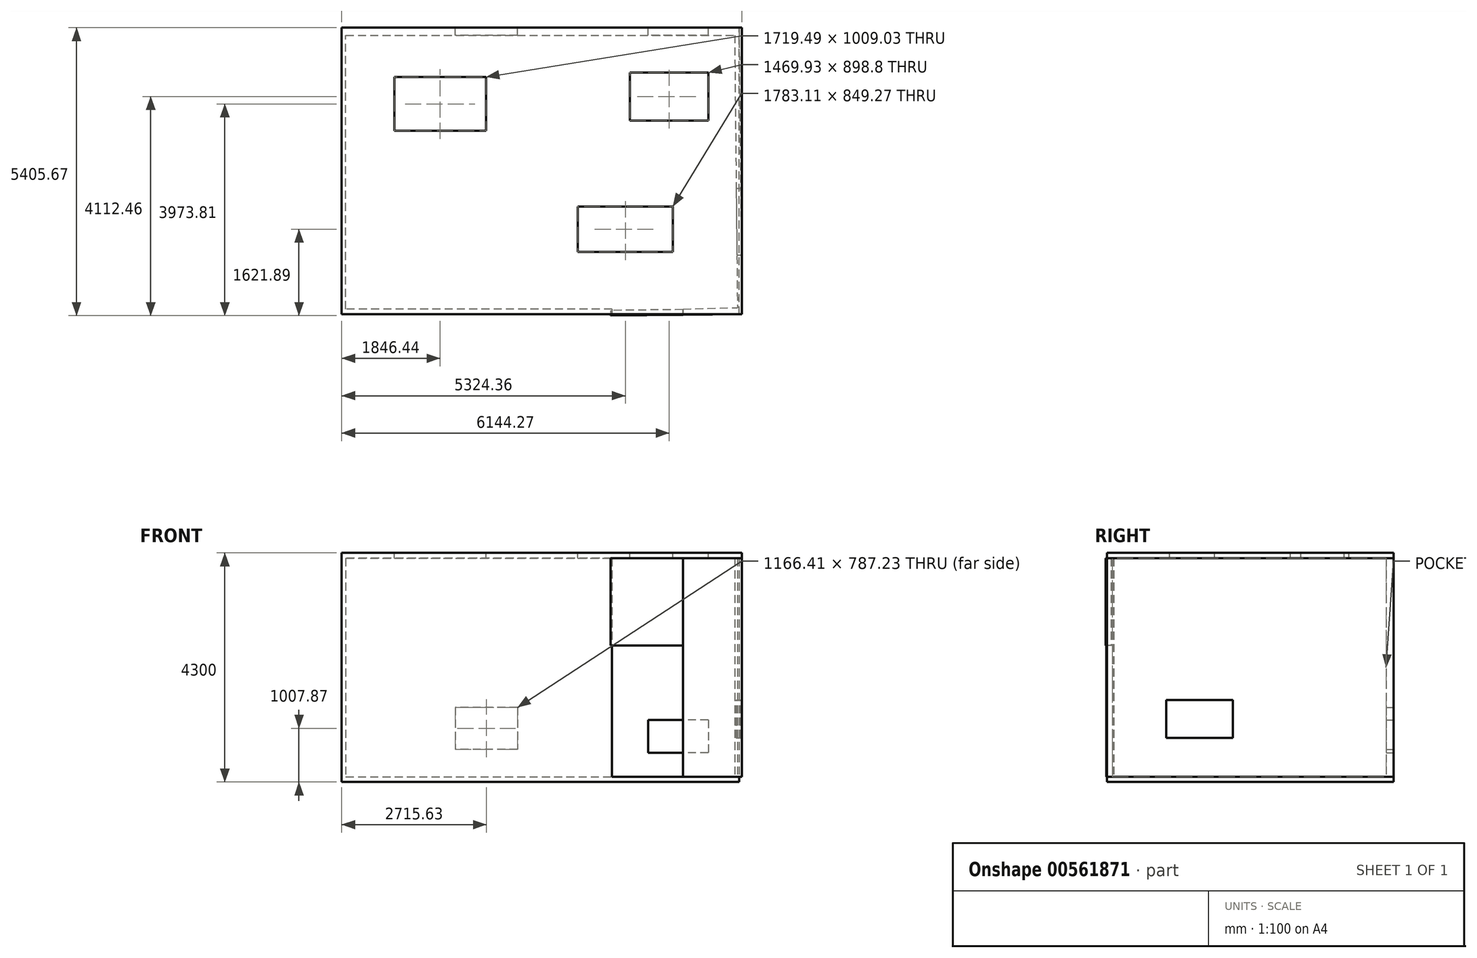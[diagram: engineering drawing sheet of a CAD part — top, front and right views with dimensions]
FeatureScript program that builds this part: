
annotation { "Feature Type Name" : "Feature", "Feature Type Description" : "" }
export const myFeature = defineFeature(function(context is Context, id is Id, definition is map)
    precondition{}
    {
        {
            var Q0;
            Q0=qCreatedBy(makeId("Top.planeOp"),FACE);
            var sketch = newSketch(context, id + "F0", { "sketchPlane" : qUnion([Q0])});
            skLineSegment(sketch, "E0", {"start": v(2012.95, -2660.95) * mm, "end": v(2012.95, -2759.71) * mm});
            skLineSegment(sketch, "E1", {"start": v(2012.95, -2759.71) * mm, "end": v(-3059.37, -2759.71) * mm});
            skLineSegment(sketch, "E2", {"start": v(-3059.37, -2759.71) * mm, "end": v(-3059.37, 2620.12) * mm});
            skLineSegment(sketch, "E3", {"start": v(-3059.37, 2620.12) * mm, "end": v(4397.09, 2620.12) * mm});
            skLineSegment(sketch, "E4", {"start": v(4397.09, 2620.12) * mm, "end": v(4453.48, -2759.71) * mm});
            skLineSegment(sketch, "E5", {"start": v(4453.48, -2759.71) * mm, "end": v(3345.91, -2771.33) * mm});
            skLineSegment(sketch, "E6", {"start": v(3345.91, -2771.33) * mm, "end": v(3345.91, -2660.95) * mm});
            skLineSegment(sketch, "E7", {"start": v(2012.95, -2660.95) * mm, "end": v(-2982.58, -2660.95) * mm});
            skLineSegment(sketch, "E8", {"start": v(-2982.58, -2660.95) * mm, "end": v(-2982.58, -764.97) * mm});
            skLineSegment(sketch, "E9", {"start": v(-2982.58, -764.97) * mm, "end": v(-2982.58, 2477.46) * mm});
            skLineSegment(sketch, "E10", {"start": v(-2982.58, 2477.46) * mm, "end": v(4314.13, 2477.46) * mm});
            skLineSegment(sketch, "E11", {"start": v(4314.13, 2477.46) * mm, "end": v(4367.73, -2634.86) * mm});
            skLineSegment(sketch, "E12", {"start": v(3345.91, -2660.95) * mm, "end": v(4367.73, -2634.86) * mm});
            skSolve(sketch);
        }
        {
            var Q0;
            Q0 = qSketchRegion(id + "F0", true);
            extrude(context, id + "F1", {"entities" : qUnion([Q0]), "depth" : 4100 * mm, "offsetDistance" : 25.4 * mm});
        }
        {
            var Q0;
            Q0=makeQuery(id+"F1.opExtrude","CAP_FACE",FACE,{"disambiguationData":[OSD([sQuery(id+"F0.wireOp",EDGE,"E0"),sQuery(id+"F0.wireOp",EDGE,"E1"),sQuery(id+"F0.wireOp",EDGE,"E2"),sQuery(id+"F0.wireOp",EDGE,"E3"),sQuery(id+"F0.wireOp",EDGE,"E4"),sQuery(id+"F0.wireOp",EDGE,"E5"),sQuery(id+"F0.wireOp",EDGE,"E6"),sQuery(id+"F0.wireOp",EDGE,"E7"),sQuery(id+"F0.wireOp",EDGE,"E8"),sQuery(id+"F0.wireOp",EDGE,"E9"),sQuery(id+"F0.wireOp",EDGE,"E10"),sQuery(id+"F0.wireOp",EDGE,"E11"),sQuery(id+"F0.wireOp",EDGE,"E12")])],"isStart":false});
            var sketch = newSketch(context, id + "F2", { "sketchPlane" : qUnion([Q0])});
            skLineSegment(sketch, "E13.bottom", {"start": v(-3059.37, 2620.12) * mm, "end": v(4453.48, 2620.12) * mm});
            skLineSegment(sketch, "E13.top", {"start": v(-3059.37, -2759.71) * mm, "end": v(4453.48, -2759.71) * mm});
            skLineSegment(sketch, "E13.left", {"start": v(-3059.37, 2620.12) * mm, "end": v(-3059.37, -2759.71) * mm});
            skLineSegment(sketch, "E13.right", {"start": v(4453.48, 2620.12) * mm, "end": v(4453.48, -2759.71) * mm});
            skSolve(sketch);
        }
        {
            var Q0;
            Q0 = qSketchRegion(id + "F2", true);
            extrude(context, id + "F3", {"entities" : qUnion([Q0]), "operationType" : NewBodyOperationType.ADD, "depth" : 100 * mm, "offsetDistance" : 25.4 * mm});
        }
        {
            var Q0;
            Q0=makeQuery(id+"F3.opExtrude","CAP_FACE",FACE,{"disambiguationData":[OSD([sQuery(id+"F2.wireOp",EDGE,"E13.bottom"),sQuery(id+"F2.wireOp",EDGE,"E13.top"),sQuery(id+"F2.wireOp",EDGE,"E13.left"),sQuery(id+"F2.wireOp",EDGE,"E13.right")])],"isStart":false});
            var sketch = newSketch(context, id + "F4", { "sketchPlane" : qUnion([Q0])});
            skLineSegment(sketch, "E14.bottom", {"start": v(1373.43, -739.03) * mm, "end": v(3156.55, -739.03) * mm});
            skLineSegment(sketch, "E14.top", {"start": v(1373.43, -1588.3) * mm, "end": v(3156.55, -1588.3) * mm});
            skLineSegment(sketch, "E14.left", {"start": v(1373.43, -739.03) * mm, "end": v(1373.43, -1588.3) * mm});
            skLineSegment(sketch, "E14.right", {"start": v(3156.55, -739.03) * mm, "end": v(3156.55, -1588.3) * mm});
            skLineSegment(sketch, "E15.bottom", {"start": v(-2072.68, 1692.78) * mm, "end": v(-353.18, 1692.78) * mm});
            skLineSegment(sketch, "E15.top", {"start": v(-2072.68, 683.75) * mm, "end": v(-353.18, 683.75) * mm});
            skLineSegment(sketch, "E15.left", {"start": v(-2072.68, 1692.78) * mm, "end": v(-2072.68, 683.75) * mm});
            skLineSegment(sketch, "E15.right", {"start": v(-353.18, 1692.78) * mm, "end": v(-353.18, 683.75) * mm});
            skLineSegment(sketch, "E16.bottom", {"start": v(2349.94, 1776.31) * mm, "end": v(3819.87, 1776.31) * mm});
            skLineSegment(sketch, "E16.top", {"start": v(2349.94, 877.5) * mm, "end": v(3819.87, 877.5) * mm});
            skLineSegment(sketch, "E16.left", {"start": v(2349.94, 1776.31) * mm, "end": v(2349.94, 877.5) * mm});
            skLineSegment(sketch, "E16.right", {"start": v(3819.87, 1776.31) * mm, "end": v(3819.87, 877.5) * mm});
            skSolve(sketch);
        }
        {
            var Q0;
            Q0 = qSketchRegion(id + "F4", true);
            extrude(context, id + "F5", {"entities" : qUnion([Q0]), "operationType" : NewBodyOperationType.REMOVE, "oppositeDirection" : true, "depth" : 2540 * mm, "offsetDistance" : 25.4 * mm});
        }
        {
            var Q0;
            Q0=makeQuery(id+"F1.opExtrude","CAP_FACE",FACE,{"disambiguationData":[OSD([sQuery(id+"F0.wireOp",EDGE,"E0"),sQuery(id+"F0.wireOp",EDGE,"E1"),sQuery(id+"F0.wireOp",EDGE,"E2"),sQuery(id+"F0.wireOp",EDGE,"E3"),sQuery(id+"F0.wireOp",EDGE,"E4"),sQuery(id+"F0.wireOp",EDGE,"E5"),sQuery(id+"F0.wireOp",EDGE,"E6"),sQuery(id+"F0.wireOp",EDGE,"E7"),sQuery(id+"F0.wireOp",EDGE,"E8"),sQuery(id+"F0.wireOp",EDGE,"E9"),sQuery(id+"F0.wireOp",EDGE,"E10"),sQuery(id+"F0.wireOp",EDGE,"E11"),sQuery(id+"F0.wireOp",EDGE,"E12")])],"isStart":true});
            var sketch = newSketch(context, id + "F6", { "sketchPlane" : qUnion([Q0])});
            skLineSegment(sketch, "E17.bottom", {"start": v(-3059.37, 2759.71) * mm, "end": v(4397.09, 2759.71) * mm});
            skLineSegment(sketch, "E17.top", {"start": v(-3059.37, -2620.12) * mm, "end": v(4397.09, -2620.12) * mm});
            skLineSegment(sketch, "E17.left", {"start": v(-3059.37, 2759.71) * mm, "end": v(-3059.37, -2620.12) * mm});
            skLineSegment(sketch, "E17.right", {"start": v(4397.09, 2759.71) * mm, "end": v(4397.09, -2620.12) * mm});
            skSolve(sketch);
        }
        {
            var Q0;
            Q0 = qSketchRegion(id + "F6", true);
            extrude(context, id + "F7", {"entities" : qUnion([Q0]), "operationType" : NewBodyOperationType.ADD, "depth" : 100 * mm, "offsetDistance" : 25.4 * mm});
        }
        {
            var Q0;
            Q0=makeQuery(id+"F1.opExtrude","SWEPT_FACE",FACE,{"disambiguationData":[OSD([sQuery(id+"F0.wireOp",EDGE,"E5")])]});
            var sketch = newSketch(context, id + "F8", { "sketchPlane" : qUnion([Q0])});
            skLineSegment(sketch, "E18.bottom", {"start": v(3316.68, 4100) * mm, "end": v(1959.7, 4100) * mm});
            skLineSegment(sketch, "E18.top", {"start": v(3316.68, 2460.04) * mm, "end": v(1959.7, 2460.04) * mm});
            skLineSegment(sketch, "E18.left", {"start": v(3316.68, 4100) * mm, "end": v(3316.68, 2460.04) * mm});
            skLineSegment(sketch, "E18.right", {"start": v(1959.7, 4100) * mm, "end": v(1959.7, 2460.04) * mm});
            skSolve(sketch);
        }
        {
            var Q0;
            Q0 = qSketchRegion(id + "F8", true);
            extrude(context, id + "F9", {"entities" : qUnion([Q0]), "oppositeDirection" : true, "depth" : 100 * mm, "offsetDistance" : 25.4 * mm});
        }
        {
            var Q0;
            Q0=makeQuery(id+"F1.opExtrude","SWEPT_FACE",FACE,{"disambiguationData":[OSD([sQuery(id+"F0.wireOp",EDGE,"E4")])]});
            var sketch = newSketch(context, id + "F10", { "sketchPlane" : qUnion([Q0])});
            skLineSegment(sketch, "E19.bottom", {"start": v(-443.84, 729.68) * mm, "end": v(-1693.33, 729.68) * mm});
            skLineSegment(sketch, "E19.top", {"start": v(-443.84, 1436.14) * mm, "end": v(-1693.33, 1436.14) * mm});
            skLineSegment(sketch, "E19.left", {"start": v(-443.84, 729.68) * mm, "end": v(-443.84, 1436.14) * mm});
            skLineSegment(sketch, "E19.right", {"start": v(-1693.33, 729.68) * mm, "end": v(-1693.33, 1436.14) * mm});
            skSolve(sketch);
        }
        {
            var Q0;
            Q0 = qSketchRegion(id + "F10", true);
            extrude(context, id + "F11", {"entities" : qUnion([Q0]), "operationType" : NewBodyOperationType.REMOVE, "oppositeDirection" : true, "depth" : 100 * mm, "offsetDistance" : 25.4 * mm});
        }
        {
            var Q0;
            Q0=makeQuery(id+"F7.boolean.opBoolean","MERGE",FACE,{"derivedFrom":[makeQuery(id+"F3.boolean.opBoolean","MERGE",FACE,{"derivedFrom":[makeQuery(id+"F1.opExtrude","SWEPT_FACE",FACE,{"disambiguationData":[OSD([sQuery(id+"F0.wireOp",EDGE,"E3")])]}),makeQuery(id+"F3.opExtrude","SWEPT_FACE",FACE,{"disambiguationData":[OSD([sQuery(id+"F2.wireOp",EDGE,"E13.bottom")])]})]}),makeQuery(id+"F7.opExtrude","SWEPT_FACE",FACE,{"disambiguationData":[OSD([sQuery(id+"F6.wireOp",EDGE,"E17.top")])]})]});
            var sketch = newSketch(context, id + "F12", { "sketchPlane" : qUnion([Q0])});
            skLineSegment(sketch, "E20.bottom", {"start": v(-3819.42, 1064.46) * mm, "end": v(-2691.43, 1064.46) * mm});
            skLineSegment(sketch, "E20.top", {"start": v(-3819.42, 447.34) * mm, "end": v(-2691.43, 447.34) * mm});
            skLineSegment(sketch, "E20.left", {"start": v(-3819.42, 1064.46) * mm, "end": v(-3819.42, 447.34) * mm});
            skLineSegment(sketch, "E20.right", {"start": v(-2691.43, 1064.46) * mm, "end": v(-2691.43, 447.34) * mm});
            skLineSegment(sketch, "E21.bottom", {"start": v(-239.46, 1301.48) * mm, "end": v(926.94, 1301.48) * mm});
            skLineSegment(sketch, "E21.top", {"start": v(-239.46, 514.25) * mm, "end": v(926.94, 514.25) * mm});
            skLineSegment(sketch, "E21.left", {"start": v(-239.46, 1301.48) * mm, "end": v(-239.46, 514.25) * mm});
            skLineSegment(sketch, "E21.right", {"start": v(926.94, 1301.48) * mm, "end": v(926.94, 514.25) * mm});
            skSolve(sketch);
        }
        {
            var Q0;
            Q0 = qSketchRegion(id + "F12", true);
            extrude(context, id + "F13", {"entities" : qUnion([Q0]), "operationType" : NewBodyOperationType.REMOVE, "oppositeDirection" : true, "depth" : 200 * mm, "offsetDistance" : 25.4 * mm});
        }
    });
